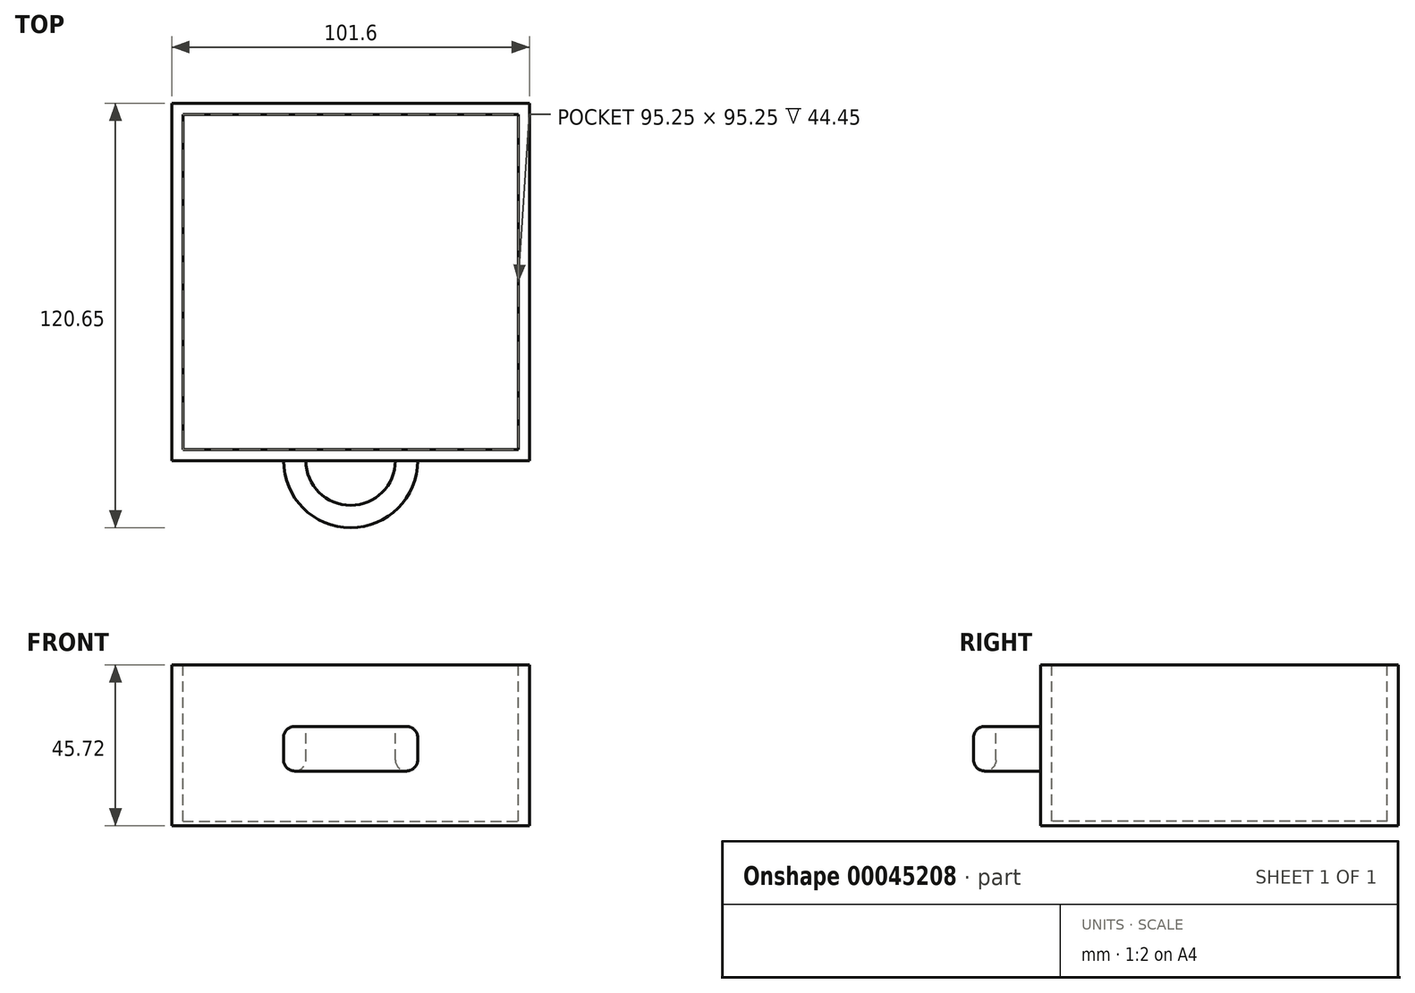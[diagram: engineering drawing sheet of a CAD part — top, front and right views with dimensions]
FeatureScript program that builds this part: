
annotation { "Feature Type Name" : "Feature", "Feature Type Description" : "" }
export const myFeature = defineFeature(function(context is Context, id is Id, definition is map)
    precondition{}
    {
        {
            var Q0;
            Q0=qCreatedBy(makeId("Front.planeOp"),FACE);
            var sketch = newSketch(context, id + "F0", { "sketchPlane" : qUnion([Q0])});
            skLineSegment(sketch, "E0.bottom", {"start": v(-33.41, 27.52) * mm, "end": v(68.19, 27.52) * mm});
            skLineSegment(sketch, "E0.top", {"start": v(-33.41, -18.2) * mm, "end": v(68.19, -18.2) * mm});
            skLineSegment(sketch, "E0.left", {"start": v(-33.41, 27.52) * mm, "end": v(-33.41, -18.2) * mm});
            skLineSegment(sketch, "E0.right", {"start": v(68.19, 27.52) * mm, "end": v(68.19, -18.2) * mm});
            skSolve(sketch);
        }
        {
            var Q0;
            Q0 = qSketchRegion(id + "F0", true);
            extrude(context, id + "F1", {"entities" : qUnion([Q0]), "oppositeDirection" : true, "depth" : 101.6 * mm});
        }
        {
            var Q0;
            Q0=makeQuery(id+"F1.opExtrude","SWEPT_FACE",FACE,{"disambiguationData":[OSD([sQuery(id+"F0.wireOp",EDGE,"E0.bottom")])]});
            var sketch = newSketch(context, id + "F2", { "sketchPlane" : qUnion([Q0])});
            skLineSegment(sketch, "E1.bottom", {"start": v(-30.24, 98.43) * mm, "end": v(65.01, 98.43) * mm});
            skLineSegment(sketch, "E1.top", {"start": v(-30.24, 3.17) * mm, "end": v(65.01, 3.18) * mm});
            skLineSegment(sketch, "E1.left", {"start": v(-30.24, 98.43) * mm, "end": v(-30.24, 3.17) * mm});
            skLineSegment(sketch, "E1.right", {"start": v(65.01, 98.43) * mm, "end": v(65.01, 3.18) * mm});
            skSolve(sketch);
        }
        {
            var Q0;
            Q0 = qSketchRegion(id + "F2", true);
            extrude(context, id + "F3", {"entities" : qUnion([Q0]), "operationType" : NewBodyOperationType.REMOVE, "oppositeDirection" : true, "depth" : 44.45 * mm});
        }
        {
            var Q0;
            Q0=makeQuery(id+"F1.opExtrude","CAP_FACE",FACE,{"disambiguationData":[OSD([sQuery(id+"F0.wireOp",EDGE,"E0.bottom"),sQuery(id+"F0.wireOp",EDGE,"E0.top"),sQuery(id+"F0.wireOp",EDGE,"E0.left"),sQuery(id+"F0.wireOp",EDGE,"E0.right")])],"isStart":true});
            var sketch = newSketch(context, id + "F4", { "sketchPlane" : qUnion([Q0])});
            skLineSegment(sketch, "E2.bottom", {"start": v(-1.66, 10.06) * mm, "end": v(36.44, 10.06) * mm});
            skLineSegment(sketch, "E2.top", {"start": v(-1.66, -2.64) * mm, "end": v(36.44, -2.64) * mm});
            skLineSegment(sketch, "E2.left", {"start": v(-1.66, 10.06) * mm, "end": v(-1.66, -2.64) * mm});
            skLineSegment(sketch, "E2.right", {"start": v(36.44, 10.06) * mm, "end": v(36.44, -2.64) * mm});
            skLineSegment(sketch, "E3", {"start": v(-1.66, 3.71) * mm, "end": v(36.44, 3.71) * mm});
            skLineSegment(sketch, "E4", {"start": v(17.39, 10.06) * mm, "end": v(17.39, -2.64) * mm});
            skSolve(sketch);
        }
        {
            var Q0;
            {var subQ3=sQuery(id+"F4.wireOp",EDGE,"E2.bottom");var subQ5=sQuery(id+"F4.wireOp",EDGE,"E2.left");var subQ7=makeQuery(id+"F4.imprint","INTERSECT",VERTEX,{"derivedFrom":[subQ3,subQ5]});Q0=makeQuery(id+"F4.imprint","IMPRINT",FACE,{"disambiguationData":[TD([[makeQuery(id+"F4.imprint","IMPRINT",EDGE,{"disambiguationData":[TD([[subQ7,-1.0]])],"derivedFrom":subQ3}),-1.0]])]});}
            var Q1;
            {var subQ3=sQuery(id+"F4.wireOp",EDGE,"E2.top");var subQ5=sQuery(id+"F4.wireOp",EDGE,"E2.left");var subQ7=makeQuery(id+"F4.imprint","INTERSECT",VERTEX,{"derivedFrom":[subQ3,subQ5]});Q1=makeQuery(id+"F4.imprint","IMPRINT",FACE,{"disambiguationData":[TD([[makeQuery(id+"F4.imprint","IMPRINT",EDGE,{"disambiguationData":[TD([[subQ7,-1.0]])],"derivedFrom":subQ3}),1.0]])]});}
            var Q2;
            Q2=sQuery(id+"F4.wireOp",EDGE,"E4");
            revolve(context, id + "F5", {"operationType" : NewBodyOperationType.ADD, "entities" : qUnion([Q0, Q1]), "axis" : qUnion([Q2]), "revolveType" : RevolveType.ONE_DIRECTION, "oppositeDirection" : true, "angle" : 180 * degree});
        }
        {
            var Q0;
            Q0=makeQuery(id+"F5.opRevolve","SWEPT_FACE",FACE,{"disambiguationData":[OSD([sQuery(id+"F4.wireOp",EDGE,"E2.bottom")])]});
            var sketch = newSketch(context, id + "F6", { "sketchPlane" : qUnion([Q0])});
            skLineSegment(sketch, "E5", {"start": v(4.69, 0) * mm, "end": v(30.09, 0) * mm});
            skArc(sketch, "E6", {"start": v(4.69, 0) * mm, "mid": v(17.39, -12.7) * mm, "end": v(30.09, 0) * mm});
            skSolve(sketch);
        }
        {
            var Q0;
            Q0 = qSketchRegion(id + "F6", true);
            extrude(context, id + "F7", {"entities" : qUnion([Q0]), "operationType" : NewBodyOperationType.REMOVE, "oppositeDirection" : true, "depth" : 25.4 * mm});
        }
        {
            var Q0;
            Q0=makeQuery(id+"F5.opRevolve","SWEPT_EDGE",EDGE,{"disambiguationData":[OSD([sQuery(id+"F4.wireOp",EDGE,"E2.bottom"),sQuery(id+"F4.wireOp",EDGE,"E2.left")])]});
            var Q1;
            Q1=makeQuery(id+"F7.boolean.opBoolean","COPY",EDGE,{"derivedFrom":makeQuery(id+"F7.opExtrude","CAP_EDGE",EDGE,{"disambiguationData":[OSD([sQuery(id+"F6.wireOp",EDGE,"E6")])],"isStart":true})});
            var Q2;
            Q2=makeQuery(id+"F5.opRevolve","SWEPT_EDGE",EDGE,{"disambiguationData":[OSD([sQuery(id+"F4.wireOp",EDGE,"E2.top"),sQuery(id+"F4.wireOp",EDGE,"E2.left")])]});
            var Q3;
            Q3=makeQuery(id+"F7.boolean.opBoolean","INTERSECT",EDGE,{"derivedFrom":[makeQuery(id+"F5.opRevolve","SWEPT_FACE",FACE,{"disambiguationData":[OSD([sQuery(id+"F4.wireOp",EDGE,"E2.top")])]}),makeQuery(id+"F7.opExtrude","SWEPT_FACE",FACE,{"disambiguationData":[OSD([sQuery(id+"F6.wireOp",EDGE,"E6")])]})]});
            fillet(context, id + "F8", {"entities" : qUnion([Q0, Q1, Q2, Q3]), "radius" : 3.17 * mm, "tangentPropagation" : true, "allowEdgeOverflow" : false});
        }
    });
